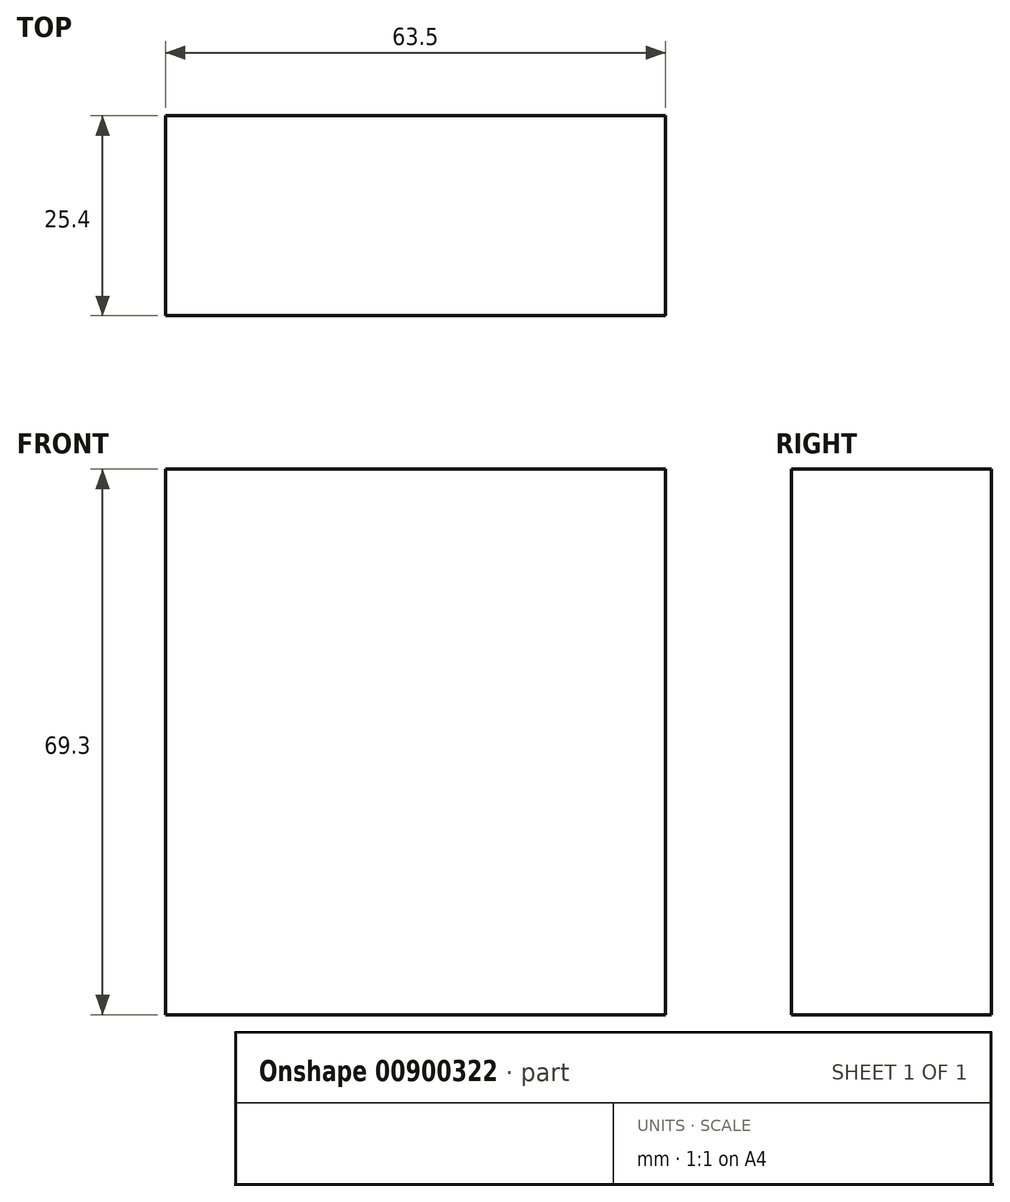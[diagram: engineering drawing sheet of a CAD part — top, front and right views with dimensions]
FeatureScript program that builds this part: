
annotation { "Feature Type Name" : "Feature", "Feature Type Description" : "" }
export const myFeature = defineFeature(function(context is Context, id is Id, definition is map)
    precondition{}
    {
        {
            var Q0;
            Q0=qCreatedBy(makeId("Front.planeOp"),FACE);
            var sketch = newSketch(context, id + "F0", { "sketchPlane" : qUnion([Q0])});
            skLineSegment(sketch, "E0.bottom", {"start": v(-31.18, 32.4) * mm, "end": v(32.32, 32.4) * mm});
            skLineSegment(sketch, "E0.top", {"start": v(-31.18, -36.9) * mm, "end": v(32.32, -36.9) * mm});
            skLineSegment(sketch, "E0.left", {"start": v(-31.18, 32.4) * mm, "end": v(-31.18, -36.9) * mm});
            skLineSegment(sketch, "E0.right", {"start": v(32.32, 32.4) * mm, "end": v(32.32, -36.9) * mm});
            skSolve(sketch);
        }
        {
            var Q0;
            Q0 = qSketchRegion(id + "F0", true);
            extrude(context, id + "F1", {"entities" : qUnion([Q0]), "depth" : 25.4 * mm, "offsetDistance" : 25.4 * mm});
        }
    });
